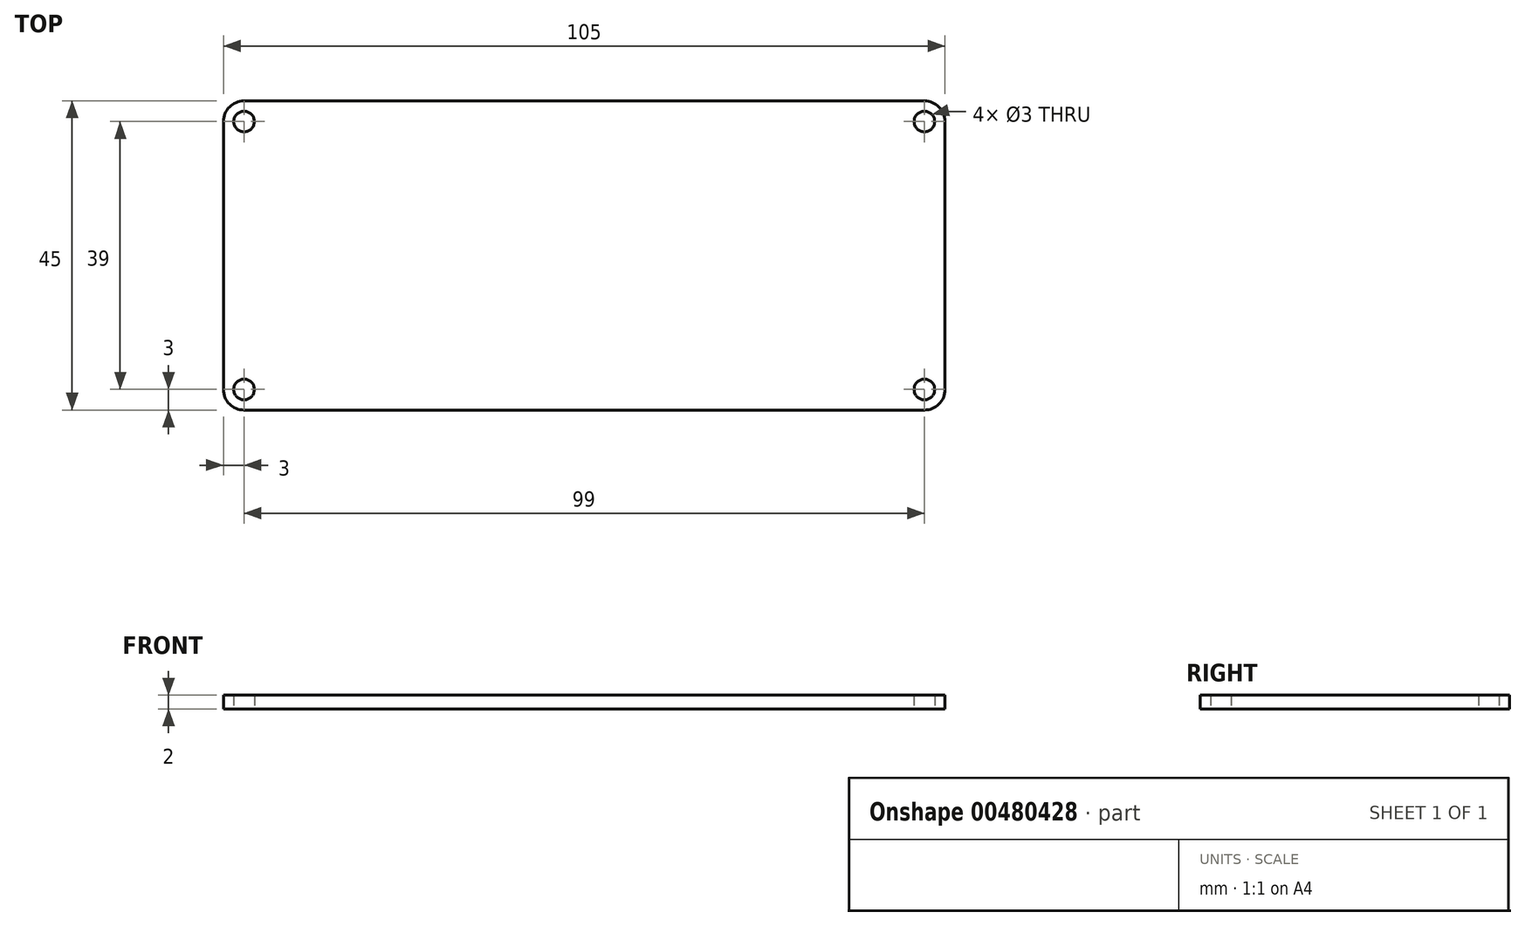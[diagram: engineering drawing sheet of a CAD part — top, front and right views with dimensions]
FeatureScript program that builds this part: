
annotation { "Feature Type Name" : "Feature", "Feature Type Description" : "" }
export const myFeature = defineFeature(function(context is Context, id is Id, definition is map)
    precondition{}
    {
        {
            var Q0;
            Q0=qCreatedBy(makeId("Top.planeOp"),FACE);
            var sketch = newSketch(context, id + "F0", { "sketchPlane" : qUnion([Q0])});
            skLineSegment(sketch, "E0.bottom", {"start": v(52.5, -22.5) * mm, "end": v(-52.5, -22.5) * mm});
            skLineSegment(sketch, "E0.top", {"start": v(52.5, 22.5) * mm, "end": v(-52.5, 22.5) * mm});
            skLineSegment(sketch, "E0.left", {"start": v(52.5, -22.5) * mm, "end": v(52.5, 22.5) * mm});
            skLineSegment(sketch, "E0.right", {"start": v(-52.5, -22.5) * mm, "end": v(-52.5, 22.5) * mm});
            skPoint(sketch, "E0.middle", {"position": v(0, 0) * mm});
            skCircle(sketch, "E1", {"center": v(-49.5, -19.5) * mm, "radius": 1.5 * mm});
            skCircle(sketch, "E2.MirrorC", {"center": v(-49.5, 19.5) * mm, "radius": 1.5 * mm});
            skCircle(sketch, "E3.MirrorC", {"center": v(49.5, 19.5) * mm, "radius": 1.5 * mm});
            skCircle(sketch, "E4.MirrorC", {"center": v(49.5, -19.5) * mm, "radius": 1.5 * mm});
            skSolve(sketch);
        }
        {
            var Q0;
            Q0 = qSketchRegion(id + "F0", true);
            extrude(context, id + "F1", {"entities" : qUnion([Q0]), "depth" : 2 * mm});
        }
        {
            var Q0;
            Q0=makeQuery(id+"F1.opExtrude","SWEPT_EDGE",EDGE,{"disambiguationData":[OSD([sQuery(id+"F0.wireOp",EDGE,"E0.bottom"),sQuery(id+"F0.wireOp",EDGE,"E0.left")])]});
            var Q1;
            Q1=makeQuery(id+"F1.opExtrude","SWEPT_EDGE",EDGE,{"disambiguationData":[OSD([sQuery(id+"F0.wireOp",EDGE,"E0.top"),sQuery(id+"F0.wireOp",EDGE,"E0.left")])]});
            var Q2;
            Q2=makeQuery(id+"F1.opExtrude","SWEPT_EDGE",EDGE,{"disambiguationData":[OSD([sQuery(id+"F0.wireOp",EDGE,"E0.bottom"),sQuery(id+"F0.wireOp",EDGE,"E0.right")])]});
            var Q3;
            Q3=makeQuery(id+"F1.opExtrude","SWEPT_EDGE",EDGE,{"disambiguationData":[OSD([sQuery(id+"F0.wireOp",EDGE,"E0.top"),sQuery(id+"F0.wireOp",EDGE,"E0.right")])]});
            fillet(context, id + "F2", {"entities" : qUnion([Q0, Q1, Q2, Q3]), "radius" : 3 * mm, "tangentPropagation" : true, "allowEdgeOverflow" : false});
        }
    });
